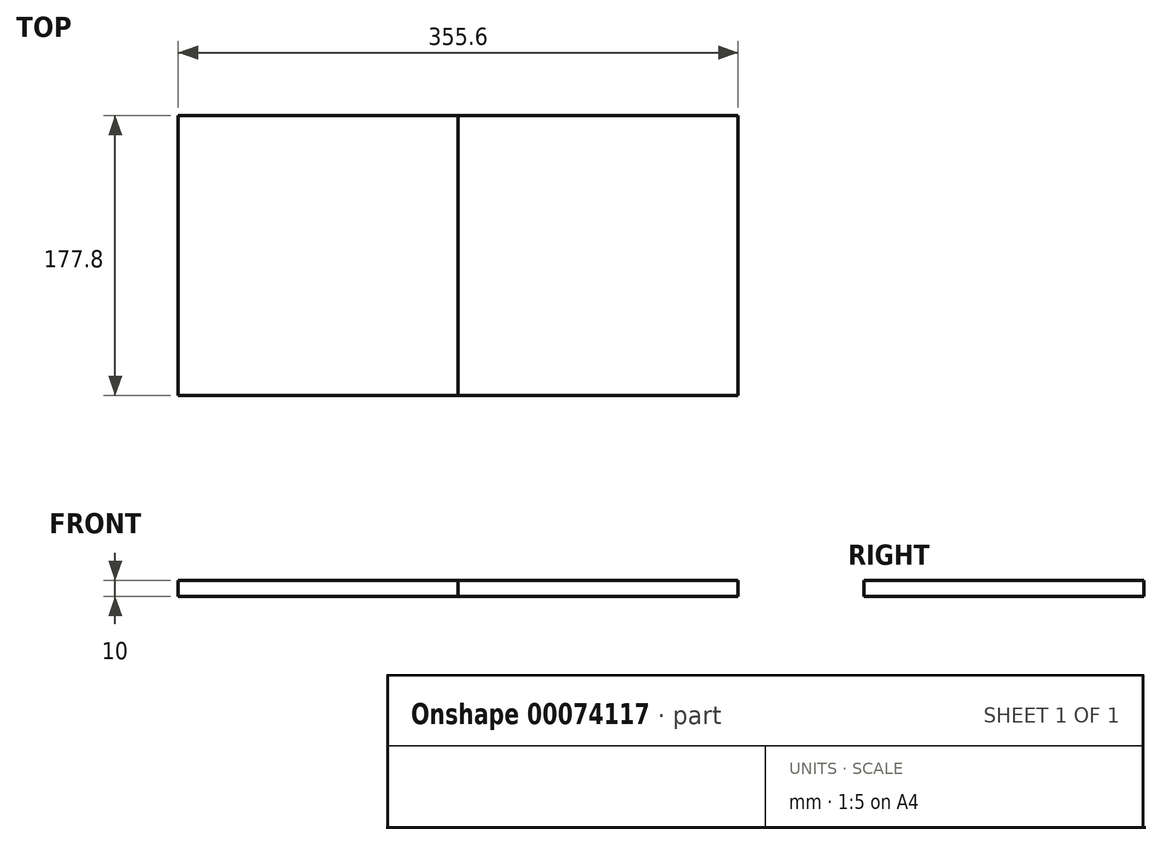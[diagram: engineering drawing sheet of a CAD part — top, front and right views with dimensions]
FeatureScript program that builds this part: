
annotation { "Feature Type Name" : "Feature", "Feature Type Description" : "" }
export const myFeature = defineFeature(function(context is Context, id is Id, definition is map)
    precondition{}
    {
        {
            var Q0;
            Q0=qCreatedBy(makeId("Top.planeOp"),FACE);
            var sketch = newSketch(context, id + "F0", { "sketchPlane" : qUnion([Q0])});
            skLineSegment(sketch, "E0.bottom", {"start": v(0, 0) * mm, "end": v(-177.8, 0) * mm});
            skLineSegment(sketch, "E0.top", {"start": v(0, -177.8) * mm, "end": v(-177.8, -177.8) * mm});
            skLineSegment(sketch, "E0.left", {"start": v(0, 0) * mm, "end": v(0, -177.8) * mm});
            skLineSegment(sketch, "E0.right", {"start": v(-177.8, 0) * mm, "end": v(-177.8, -177.8) * mm});
            skLineSegment(sketch, "E1.bottom", {"start": v(0, 0) * mm, "end": v(177.8, 0) * mm});
            skLineSegment(sketch, "E1.top", {"start": v(0, -177.8) * mm, "end": v(177.8, -177.8) * mm});
            skLineSegment(sketch, "E1.right", {"start": v(177.8, 0) * mm, "end": v(177.8, -177.8) * mm});
            skSolve(sketch);
        }
        {
            var Q0;
            Q0=makeQuery(id+"F0.imprint","IMPRINT",FACE,{"disambiguationData":[TD([[makeQuery(id+"F0.imprint","IMPRINT",EDGE,{"derivedFrom":sQuery(id+"F0.wireOp",EDGE,"E0.bottom")}),1.0]])]});
            extrude(context, id + "F1", {"entities" : qUnion([Q0]), "depth" : 10 * mm});
        }
        {
            var Q0;
            Q0=makeQuery(id+"F0.imprint","IMPRINT",FACE,{"disambiguationData":[TD([[makeQuery(id+"F0.imprint","IMPRINT",EDGE,{"derivedFrom":sQuery(id+"F0.wireOp",EDGE,"E1.bottom")}),-1.0]])]});
            extrude(context, id + "F2", {"entities" : qUnion([Q0]), "depth" : 10 * mm});
        }
    });
